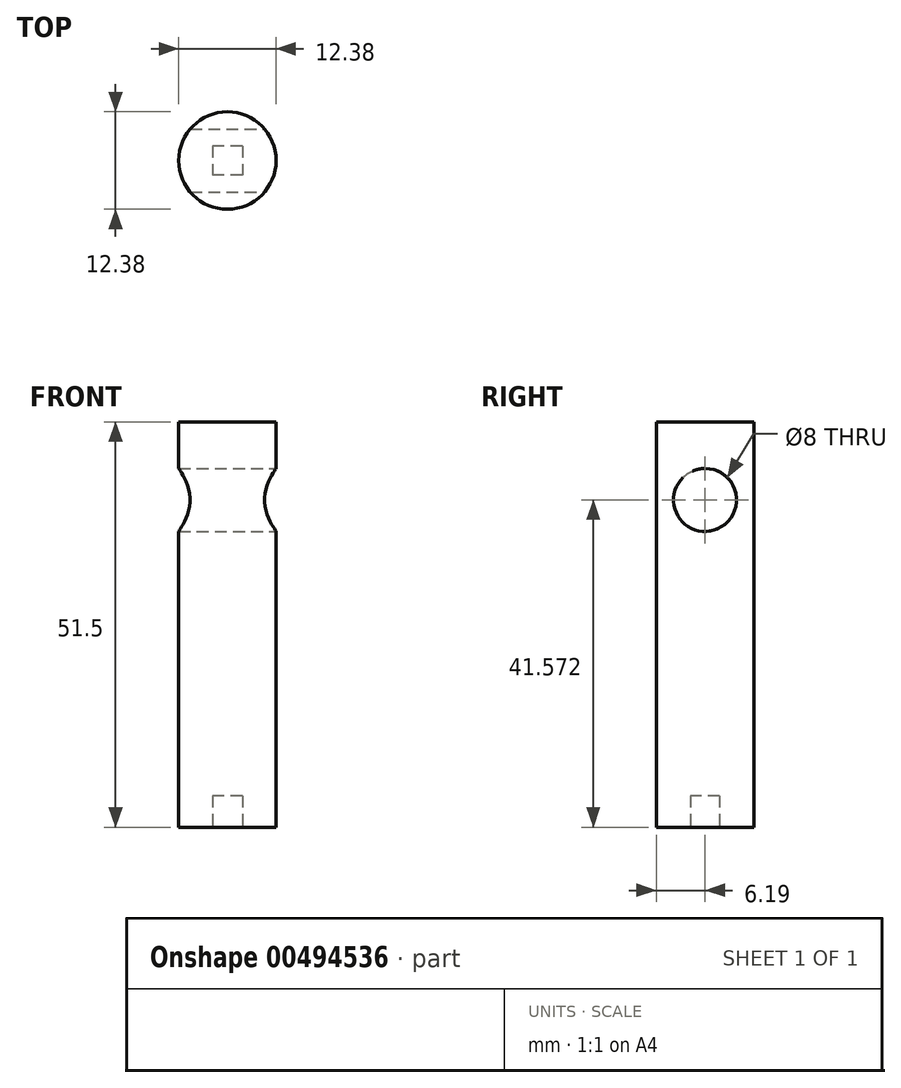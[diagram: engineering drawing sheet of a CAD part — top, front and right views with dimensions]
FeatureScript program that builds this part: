
annotation { "Feature Type Name" : "Feature", "Feature Type Description" : "" }
export const myFeature = defineFeature(function(context is Context, id is Id, definition is map)
    precondition{}
    {
        {
            var Q0;
            Q0=qCreatedBy(makeId("Top.planeOp"),FACE);
            var sketch = newSketch(context, id + "F0", { "sketchPlane" : qUnion([Q0])});
            skCircle(sketch, "E0", {"center": v(0, 0) * mm, "radius": 6.19 * mm});
            skSolve(sketch);
        }
        {
            var Q0;
            Q0=makeQuery(id+"F0.imprint","IMPRINT",FACE,{"disambiguationData":[TD([[makeQuery(id+"F0.imprint","IMPRINT",EDGE,{"derivedFrom":sQuery(id+"F0.wireOp",EDGE,"E0")}),1.0]])]});
            extrude(context, id + "F1", {"entities" : qUnion([Q0]), "depth" : 51.5 * mm});
        }
        {
            var Q0;
            Q0=qCreatedBy(makeId("Right.planeOp"),FACE);
            var sketch = newSketch(context, id + "F2", { "sketchPlane" : qUnion([Q0])});
            skCircle(sketch, "E1", {"center": v(0, 41.57) * mm, "radius": 4.12 * mm});
            skSolve(sketch);
        }
        {
            var Q0;
            Q0=sQuery(id+"F2.wireOp",VERTEX,"E1.center");
            var Q1;
            Q1=makeQuery(id+"F1.opExtrude","SWEPT_BODY",BODY,{"disambiguationData":[OSD([sQuery(id+"F0.wireOp",EDGE,"E0")])]});
            hole(context, id + "F3", {"style" : HoleStyle.SIMPLE, "endStyle" : HoleEndStyle.THROUGH, "holeDiameter" : 8 * mm, "isTappedThrough" : true, "tappedDepth" : 12 * mm, "tapClearance" : 3, "locations" : qUnion([Q0]), "scope" : qUnion([Q1])});
        }
        {
            var Q0;
            Q0=sQuery(id+"F2.wireOp",VERTEX,"E1.center");
            var Q1;
            Q1=makeQuery(id+"F1.opExtrude","SWEPT_BODY",BODY,{"disambiguationData":[OSD([sQuery(id+"F0.wireOp",EDGE,"E0")])]});
            hole(context, id + "F4", {"style" : HoleStyle.SIMPLE, "endStyle" : HoleEndStyle.THROUGH, "oppositeDirection" : true, "holeDiameter" : 8 * mm, "isTappedThrough" : true, "tappedDepth" : 12 * mm, "tapClearance" : 3, "locations" : qUnion([Q0]), "scope" : qUnion([Q1])});
        }
        {
            var Q0;
            Q0=qCreatedBy(makeId("Top.planeOp"),FACE);
            var sketch = newSketch(context, id + "F5", { "sketchPlane" : qUnion([Q0])});
            skLineSegment(sketch, "E2.bottom", {"start": v(1.9, 1.85) * mm, "end": v(-1.9, 1.85) * mm});
            skLineSegment(sketch, "E2.top", {"start": v(1.9, -1.85) * mm, "end": v(-1.9, -1.85) * mm});
            skLineSegment(sketch, "E2.left", {"start": v(1.9, 1.85) * mm, "end": v(1.9, -1.85) * mm});
            skLineSegment(sketch, "E2.right", {"start": v(-1.9, 1.85) * mm, "end": v(-1.9, -1.85) * mm});
            skPoint(sketch, "E2.middle", {"position": v(0, 0) * mm});
            skSolve(sketch);
        }
        {
            var Q0;
            Q0=makeQuery(id+"F5.imprint","IMPRINT",FACE,{"disambiguationData":[TD([[makeQuery(id+"F5.imprint","IMPRINT",EDGE,{"derivedFrom":sQuery(id+"F5.wireOp",EDGE,"E2.bottom")}),1.0]])]});
            extrude(context, id + "F6", {"entities" : qUnion([Q0]), "operationType" : NewBodyOperationType.REMOVE, "depth" : 4 * mm});
        }
    });
